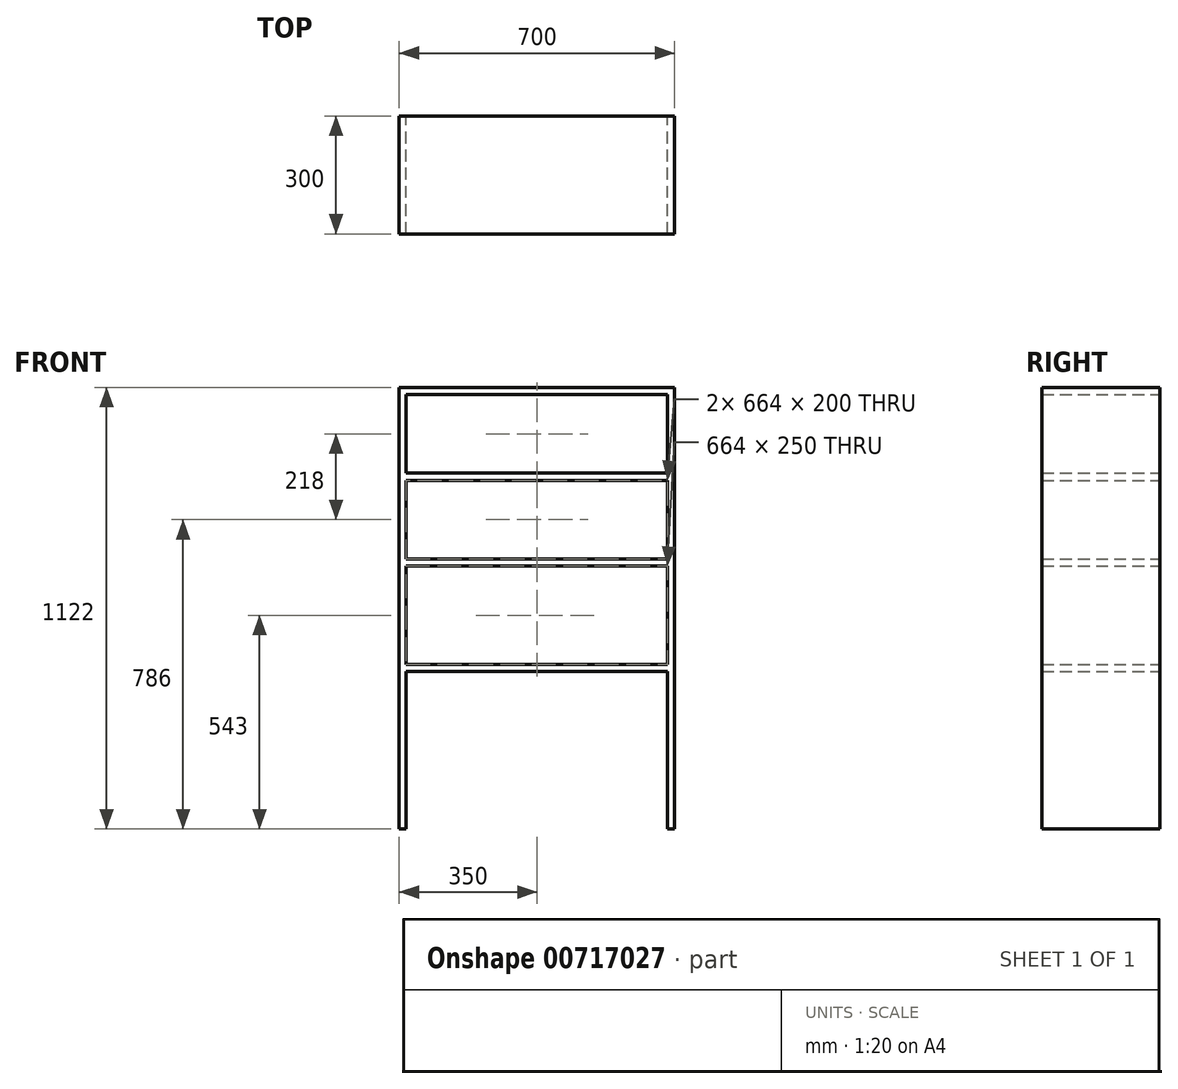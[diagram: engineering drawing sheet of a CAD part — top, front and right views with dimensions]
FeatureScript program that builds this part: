
annotation { "Feature Type Name" : "Feature", "Feature Type Description" : "" }
export const myFeature = defineFeature(function(context is Context, id is Id, definition is map)
    precondition{}
    {
        {
            var Q0;
            Q0=qCreatedBy(makeId("Front.planeOp"),FACE);
            var sketch = newSketch(context, id + "F0", { "sketchPlane" : qUnion([Q0])});
            skLineSegment(sketch, "E0.bottom", {"start": v(0, 0) * mm, "end": v(18, 0) * mm});
            skLineSegment(sketch, "E0.left", {"start": v(0, 0) * mm, "end": v(0, 1122) * mm});
            skLineSegment(sketch, "E0.right", {"start": v(18, 0) * mm, "end": v(18, 400) * mm});
            skLineSegment(sketch, "E1.bottom", {"start": v(682, 0) * mm, "end": v(700, 0) * mm});
            skLineSegment(sketch, "E1.left", {"start": v(682, 0) * mm, "end": v(682, 400) * mm});
            skLineSegment(sketch, "E1.right", {"start": v(700, 0) * mm, "end": v(700, 1122) * mm});
            skLineSegment(sketch, "E2.bottom", {"start": v(18, 418) * mm, "end": v(682, 418) * mm});
            skLineSegment(sketch, "E2.top", {"start": v(18, 400) * mm, "end": v(682, 400) * mm});
            skLineSegment(sketch, "E3.bottom", {"start": v(18, 668) * mm, "end": v(682, 668) * mm});
            skLineSegment(sketch, "E3.top", {"start": v(18, 686) * mm, "end": v(682, 686) * mm});
            skLineSegment(sketch, "E4.bottom", {"start": v(18, 886) * mm, "end": v(682, 886) * mm});
            skLineSegment(sketch, "E4.top", {"start": v(18, 904) * mm, "end": v(682, 904) * mm});
            skLineSegment(sketch, "E5.bottom", {"start": v(18, 1104) * mm, "end": v(682, 1104) * mm});
            skLineSegment(sketch, "E5.top", {"start": v(18, 1122) * mm, "end": v(682, 1122) * mm});
            skLineSegment(sketch, "E6.trimOffspring", {"start": v(18, 904) * mm, "end": v(18, 1104) * mm});
            skLineSegment(sketch, "E7.trimOffspring", {"start": v(682, 904) * mm, "end": v(682, 1104) * mm});
            skLineSegment(sketch, "E8.trimOffspring", {"start": v(18, 686) * mm, "end": v(18, 886) * mm});
            skLineSegment(sketch, "E9.trimOffspring", {"start": v(682, 686) * mm, "end": v(682, 886) * mm});
            skLineSegment(sketch, "E10.trimOffspring", {"start": v(682, 418) * mm, "end": v(682, 668) * mm});
            skLineSegment(sketch, "E11.trimOffspring", {"start": v(18, 418) * mm, "end": v(18, 668) * mm});
            skLineSegment(sketch, "E12", {"start": v(18, 1122) * mm, "end": v(0, 1122) * mm});
            skLineSegment(sketch, "E13", {"start": v(682, 1122) * mm, "end": v(700, 1122) * mm});
            skPoint(sketch, "E14.start.orphan", {"position": v(18, 1200) * mm});
            skPoint(sketch, "E15.orphan", {"position": v(700, 1200) * mm});
            skSolve(sketch);
        }
        {
            var Q0;
            Q0=makeQuery(id+"F0.imprint","IMPRINT",FACE,{"disambiguationData":[TD([[makeQuery(id+"F0.imprint","IMPRINT",EDGE,{"derivedFrom":sQuery(id+"F0.wireOp",EDGE,"E0.bottom")}),1.0]])]});
            extrude(context, id + "F1", {"entities" : qUnion([Q0]), "depth" : 300 * mm, "offsetDistance" : 25 * mm});
        }
    });
